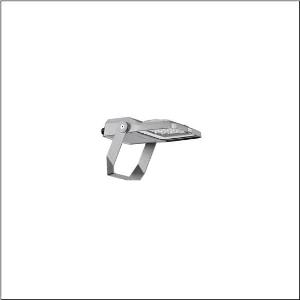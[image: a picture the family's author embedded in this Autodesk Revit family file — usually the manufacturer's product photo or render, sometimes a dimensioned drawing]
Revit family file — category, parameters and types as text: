
# Revit family: floodlight_fl_21_iq_micro___rs12_5xa7761a2b1a_22b8
name_source: partatom
category: Lighting Fixtures
units: mm (PartAtom-declared; Revit-internal decimal feet)

## family parameters
Cut with Voids When Loaded = No
Host = Face
Light Source = No
Part Type = Normal
Room Calculation Point = No
Round Connector Dimension = Use Diameter
Shared = No

## types (1)
- --- (1 x LED, 3090 lm, 23.1 W, 3000K)
    Apparent Load = 23 VA
    CIE Flux Codes = 79 92 99 100 100
    Color Rendering = 70
    Color Temperature = 3000K
    Default Elevation = 1800 mm
    Description = Floodlight FL 21 iQ micro, floodlight, primary light control with lens, of PMMA, primary optical cover: protective disc, of toughened safety glass, transparent, light distribution: RS12, light emission: direct distribution, installation type: surface-mounted, LED, High Power LED, rated luminous flux: 3.090lm, luminous efficacy: 134lm/W, light colour: 730, colour temperature: 3000K, control: optimised constant luminous flux control (CLO 2.0), Desk-Remote (wireless, voltage-free reading and setting of iQ features in the workshop via application-optimized NFC function/RFID function), Light-Fading, Smart-Wire, Night-Set, Lumen-Switch, Temp-Guard, Auto-Match, with terminal, 6-pole, mains connection: 220..240V, AC, 50/60Hz, start of lifetime: 23W, end of service life: 24W, reduction: 11W, luminaire housing, of diecast aluminium, powder-coated, Siteco® metallic grey (DB 702S), corrosivity category C5 mid according to DIN EN ISO 12944, sealing non-destructively replaceable, mounting bracket, of steel, galvanised, powder-coated, Siteco® metallic grey (DB 702S), protection rating (complete): IP66, insulation class (complete): insulation class II (safety insulation), certification: CE, ENEC, VDE, protection symbol: D, impact resistance: IK07, permissible operating ambient temperature: -40..+40°C, permissible operating ambient temperature for outdoor applications: -40..+50°C, standard: DIN EN 12944, LABS conformity tested according to VDMA 24364:2018-05, packaging unit: 1 piece

Light Distribution: RS12
    Height = 65 mm
    Lamp = 1 x LED
    Lamp Light Flux = 3090 lm
    Lamp Power = 23.1 W
    Lamp count = 1
    Length = 312 mm
    Luminous efficacy = 134 lm/W
    Manufacturer = Siteco
    ModVariant = No
    Model = 5XA7761A2B1A
    Mounting Place = Wall
    Mounting Type = Surface mounted
    Number of Poles = 1
    OnlyDefault = Yes
    Power Factor = 1
    Product Name = Floodlight FL 21 iQ micro | RS12
    Product group = floodlight | wall mounted
    ProductGroupID = 2001
    Protection Class = Protection class II
    Protection Degree = IP 66
    RLX_Detail_Level = 1
    RLX_Emergency_Light_Flux = 0 lm
    RLX_Emergency_Type = 0
    RLX_Emergency_Type_DB = No
    RlxData = <blob elided: 74901 chars, md5=d3c7a1dd>
    Socket = socket
    Standby Power = 0 W
    System Light Flux = 3090 lm
    System Power = 23 W
    Type Comments = factory setting: luminous flux: 100 % | dim-lin: 254 | 455 mA
    Type Image = l_1006880.jpg
    URL = http://relux.com
    VarID = @adj_115045
    Voltage = 0 V
    Weight = 0.00 kg
    Width = 230 mm

## geometry (parser evidence)
native form markers: Blend x4, Sweep x11
no freeform markers — native parametric forms only
